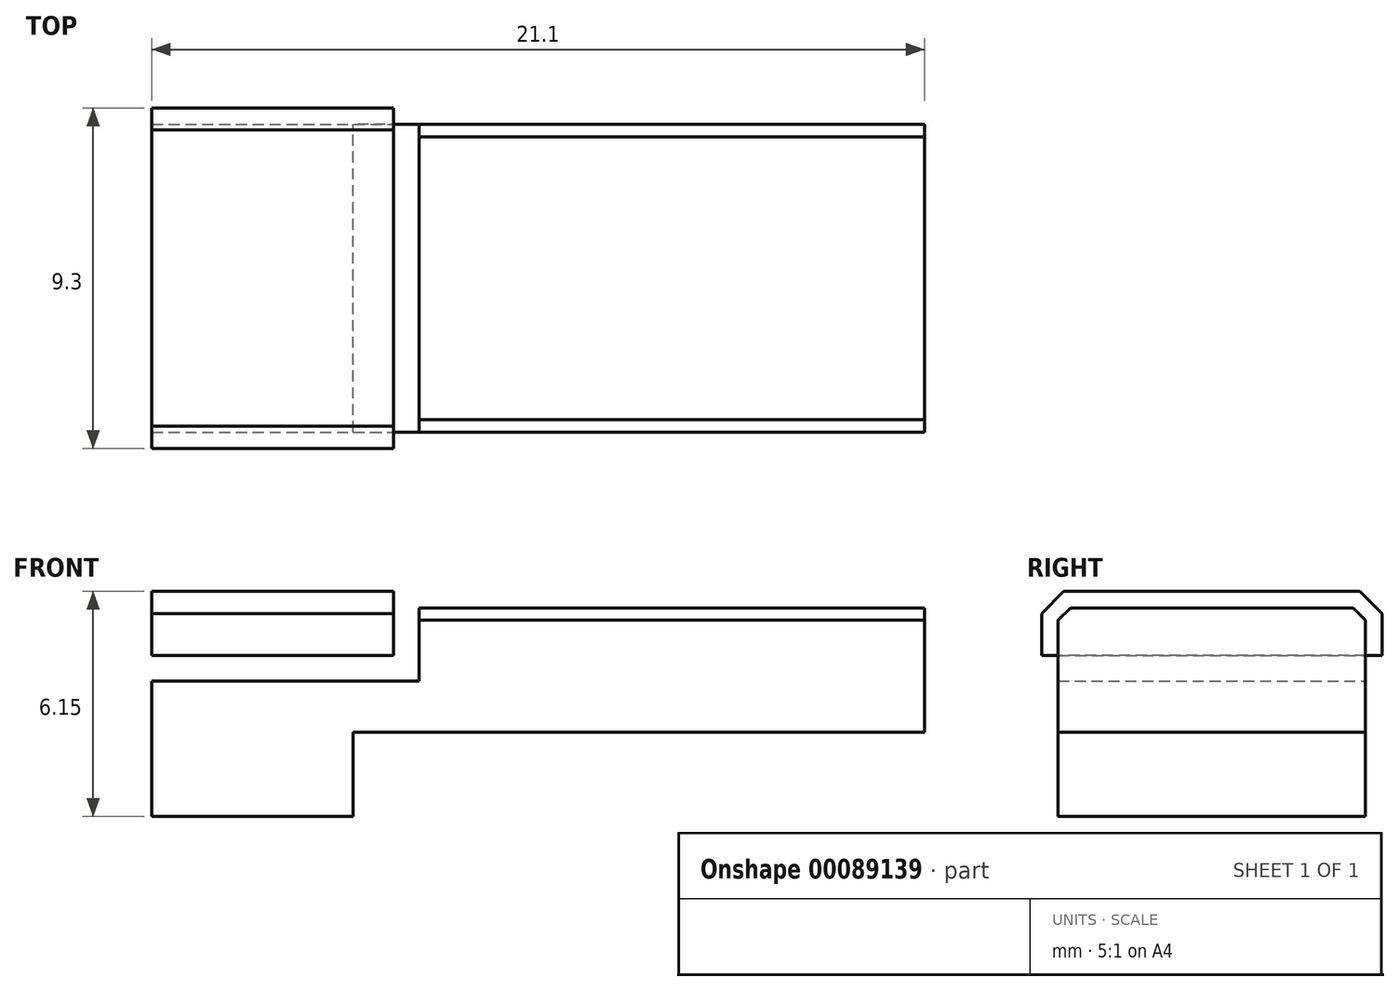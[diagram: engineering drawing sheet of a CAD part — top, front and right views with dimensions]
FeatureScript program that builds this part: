
annotation { "Feature Type Name" : "Feature", "Feature Type Description" : "" }
export const myFeature = defineFeature(function(context is Context, id is Id, definition is map)
    precondition{}
    {
        {
            var Q0;
            Q0=qCreatedBy(makeId("Top.planeOp"),FACE);
            var sketch = newSketch(context, id + "F0", { "sketchPlane" : qUnion([Q0])});
            skLineSegment(sketch, "E0.bottom", {"start": v(0, -4.9) * mm, "end": v(23, -4.9) * mm});
            skLineSegment(sketch, "E0.top", {"start": v(0, 4.9) * mm, "end": v(23, 4.9) * mm});
            skLineSegment(sketch, "E0.left", {"start": v(0, -4.9) * mm, "end": v(0, 4.9) * mm});
            skLineSegment(sketch, "E0.right", {"start": v(23, -4.9) * mm, "end": v(23, 4.9) * mm});
            skSolve(sketch);
        }
        {
            var Q0;
            Q0 = qSketchRegion(id + "F0", true);
            extrude(context, id + "F1", {"entities" : qUnion([Q0]), "depth" : 5.1 * mm});
        }
        {
            var Q0;
            Q0=makeQuery(id+"F1.opExtrude","CAP_FACE",FACE,{"disambiguationData":[OSD([sQuery(id+"F0.wireOp",EDGE,"E0.bottom"),sQuery(id+"F0.wireOp",EDGE,"E0.top"),sQuery(id+"F0.wireOp",EDGE,"E0.left"),sQuery(id+"F0.wireOp",EDGE,"E0.right")])],"isStart":false});
            var sketch = newSketch(context, id + "F2", { "sketchPlane" : qUnion([Q0])});
            skLineSegment(sketch, "E1.top", {"start": v(23, -4.9) * mm, "end": v(7.3, -4.9) * mm});
            skLineSegment(sketch, "E1.left", {"start": v(23, 4.9) * mm, "end": v(23, -4.9) * mm});
            skLineSegment(sketch, "E1.right", {"start": v(7.3, 4.9) * mm, "end": v(7.3, -4.9) * mm});
            skLineSegment(sketch, "E2.0", {"start": v(0, -4.9) * mm, "end": v(0, 4.9) * mm, "construction": true});
            skSolve(sketch);
        }
        {
            var Q0;
            Q0=makeQuery(id+"F2.imprint","IMPRINT",FACE,{"disambiguationData":[TD([[makeQuery(id+"F2.imprint","IMPRINT",EDGE,{"derivedFrom":sQuery(id+"F2.wireOp",EDGE,"E1.top")}),1.0]])]});
            extrude(context, id + "F3", {"entities" : qUnion([Q0]), "operationType" : NewBodyOperationType.ADD, "depth" : 2 * mm});
        }
        {
            var Q0;
            Q0=makeQuery(id+"F1.opExtrude","CAP_FACE",FACE,{"disambiguationData":[OSD([sQuery(id+"F0.wireOp",EDGE,"E0.bottom"),sQuery(id+"F0.wireOp",EDGE,"E0.top"),sQuery(id+"F0.wireOp",EDGE,"E0.left"),sQuery(id+"F0.wireOp",EDGE,"E0.right")])],"isStart":true});
            var sketch = newSketch(context, id + "F4", { "sketchPlane" : qUnion([Q0])});
            skLineSegment(sketch, "E3.bottom", {"start": v(6.2, 4.5) * mm, "end": v(22.2, 4.5) * mm});
            skLineSegment(sketch, "E3.top", {"start": v(6.2, -4.5) * mm, "end": v(22.2, -4.5) * mm});
            skLineSegment(sketch, "E3.left", {"start": v(6.2, 4.5) * mm, "end": v(6.2, -4.5) * mm});
            skLineSegment(sketch, "E3.right", {"start": v(22.2, 4.5) * mm, "end": v(22.2, -4.5) * mm});
            skSolve(sketch);
        }
        {
            var Q0;
            Q0 = qSketchRegion(id + "F4", true);
            extrude(context, id + "F5", {"entities" : qUnion([Q0]), "operationType" : NewBodyOperationType.REMOVE, "oppositeDirection" : true, "depth" : 3 * mm});
        }
        {
            var Q0;
            Q0=makeQuery(id+"F3.opExtrude","CAP_EDGE",EDGE,{"disambiguationData":[OSD([sQuery(id+"F2.wireOp",EDGE,"E1.top")])],"isStart":false});
            var Q1;
            Q1=makeQuery(id+"F3.opExtrude","CAP_EDGE",EDGE,{"disambiguationData":[OSD([sQuery(id+"F0.wireOp",EDGE,"E0.top")])],"isStart":false});
            chamfer(context, id + "F6", {"entities" : qUnion([Q0, Q1]), "width" : 0.75 * mm, "tangentPropagation" : true});
        }
        {
            var Q0;
            Q0=makeQuery(id+"F5.boolean.opBoolean","COPY",FACE,{"derivedFrom":makeQuery(id+"F5.opExtrude","CAP_FACE",FACE,{"disambiguationData":[OSD([sQuery(id+"F4.wireOp",EDGE,"E3.bottom"),sQuery(id+"F4.wireOp",EDGE,"E3.top"),sQuery(id+"F4.wireOp",EDGE,"E3.left"),sQuery(id+"F4.wireOp",EDGE,"E3.right")])],"isStart":false})});
            var Q1;
            Q1=makeQuery(id+"F5.boolean.opBoolean","COPY",FACE,{"derivedFrom":makeQuery(id+"F5.opExtrude","SWEPT_FACE",FACE,{"disambiguationData":[OSD([sQuery(id+"F4.wireOp",EDGE,"E3.left")])]})});
            shell(context, id + "F7", {"entities" : qUnion([Q0, Q1]), "thickness" : .7 * mm});
        }
        {
            var Q0;
            Q0=makeQuery(id+"F1.opExtrude","SWEPT_FACE",FACE,{"disambiguationData":[OSD([sQuery(id+"F0.wireOp",EDGE,"E0.left")])]});
            var sketch = newSketch(context, id + "F8", { "sketchPlane" : qUnion([Q0])});
            skCircle(sketch, "E4", {"center": v(-1.5, 3.4) * mm, "radius": 0.3 * mm});
            skCircle(sketch, "E5", {"center": v(1.5, 3.4) * mm, "radius": 0.3 * mm});
            skPoint(sketch, "E6", {"position": v(-1.52, 3.7) * mm});
            skPoint(sketch, "E7", {"position": v(1.52, 3.7) * mm});
            skSolve(sketch);
        }
        {
            var Q0;
            Q0 = qSketchRegion(id + "F8", true);
            extrude(context, id + "F9", {"entities" : qUnion([Q0]), "operationType" : NewBodyOperationType.REMOVE, "endBound" : BoundingType.UP_TO_NEXT, "oppositeDirection" : true, "depth" : 25 * mm});
        }
        {
            var Q0;
            Q0=makeQuery(id+"F1.opExtrude","CAP_EDGE",EDGE,{"disambiguationData":[OSD([sQuery(id+"F0.wireOp",EDGE,"E0.top")])],"isStart":true});
            var Q1;
            Q1=makeQuery(id+"F1.opExtrude","CAP_EDGE",EDGE,{"disambiguationData":[OSD([sQuery(id+"F0.wireOp",EDGE,"E0.bottom")])],"isStart":true});
            var Q2;
            Q2=makeQuery(id+"F1.opExtrude","CAP_EDGE",EDGE,{"disambiguationData":[OSD([sQuery(id+"F0.wireOp",EDGE,"E0.left")])],"isStart":false});
            var Q3;
            Q3=makeQuery(id+"F3.opExtrude","CAP_EDGE",EDGE,{"disambiguationData":[OSD([sQuery(id+"F2.wireOp",EDGE,"E1.right")])],"isStart":false});
            var Q4;
            Q4=makeQuery(id+"F1.opExtrude","CAP_EDGE",EDGE,{"disambiguationData":[OSD([sQuery(id+"F0.wireOp",EDGE,"E0.bottom")])],"isStart":false});
            var Q5;
            Q5=makeQuery(id+"F1.opExtrude","CAP_EDGE",EDGE,{"disambiguationData":[OSD([sQuery(id+"F0.wireOp",EDGE,"E0.top")])],"isStart":false});
            var Q6;
            Q6=makeQuery(id+"F3.opExtrude","SWEPT_EDGE",EDGE,{"disambiguationData":[OSD([sQuery(id+"F0.wireOp",EDGE,"E0.top"),sQuery(id+"F2.wireOp",EDGE,"E1.right")])]});
            var Q7;
            Q7=makeQuery(id+"F3.opExtrude","SWEPT_EDGE",EDGE,{"disambiguationData":[OSD([sQuery(id+"F0.wireOp",EDGE,"E0.bottom"),sQuery(id+"F2.wireOp",EDGE,"E1.top"),sQuery(id+"F2.wireOp",EDGE,"E1.right")])]});
            var Q8;
            Q8=makeQuery(id+"F6.opChamfer","BLEND_EDGE",EDGE,{"blendedFrom":[makeQuery(id+"F3.opExtrude","CAP_EDGE",EDGE,{"disambiguationData":[OSD([sQuery(id+"F0.wireOp",EDGE,"E0.top")])],"isStart":false}),makeQuery(id+"F3.opExtrude","SWEPT_FACE",FACE,{"disambiguationData":[OSD([sQuery(id+"F2.wireOp",EDGE,"E1.right")])]})],"blendedInto":[makeQuery(id+"F3.opExtrude","SWEPT_FACE",FACE,{"disambiguationData":[OSD([sQuery(id+"F2.wireOp",EDGE,"E1.right")])]})]});
            var Q9;
            Q9=makeQuery(id+"F6.opChamfer","BLEND_EDGE",EDGE,{"blendedFrom":[makeQuery(id+"F3.opExtrude","CAP_EDGE",EDGE,{"disambiguationData":[OSD([sQuery(id+"F2.wireOp",EDGE,"E1.top")])],"isStart":false}),makeQuery(id+"F3.opExtrude","SWEPT_FACE",FACE,{"disambiguationData":[OSD([sQuery(id+"F2.wireOp",EDGE,"E1.right")])]})],"blendedInto":[makeQuery(id+"F3.opExtrude","SWEPT_FACE",FACE,{"disambiguationData":[OSD([sQuery(id+"F2.wireOp",EDGE,"E1.right")])]})]});
            var Q10;
            Q10=makeQuery(id+"F1.opExtrude","SWEPT_EDGE",EDGE,{"disambiguationData":[OSD([sQuery(id+"F0.wireOp",EDGE,"E0.bottom"),sQuery(id+"F0.wireOp",EDGE,"E0.left")])]});
            var Q11;
            Q11=makeQuery(id+"F1.opExtrude","SWEPT_EDGE",EDGE,{"disambiguationData":[OSD([sQuery(id+"F0.wireOp",EDGE,"E0.top"),sQuery(id+"F0.wireOp",EDGE,"E0.left")])]});
            var Q12;
            Q12=makeQuery(id+"F3.boolean.opBoolean","MERGE",FACE,{"derivedFrom":[makeQuery(id+"F1.opExtrude","SWEPT_FACE",FACE,{"disambiguationData":[OSD([sQuery(id+"F0.wireOp",EDGE,"E0.right")])]}),makeQuery(id+"F3.opExtrude","SWEPT_FACE",FACE,{"disambiguationData":[OSD([sQuery(id+"F2.wireOp",EDGE,"E1.left")])]})]});
            var Q13;
            Q13=makeQuery(id+"F1.opExtrude","CAP_FACE",FACE,{"disambiguationData":[OSD([sQuery(id+"F0.wireOp",EDGE,"E0.bottom"),sQuery(id+"F0.wireOp",EDGE,"E0.top"),sQuery(id+"F0.wireOp",EDGE,"E0.left"),sQuery(id+"F0.wireOp",EDGE,"E0.right")])],"isStart":true});
            var Q14;
            Q14=makeQuery(id+"F3.opExtrude","CAP_EDGE",EDGE,{"disambiguationData":[OSD([sQuery(id+"F2.wireOp",EDGE,"E1.right")])],"isStart":true});
            chamfer(context, id + "F10", {"entities" : qUnion([Q0, Q1, Q2, Q3, Q4, Q5, Q6, Q7, Q8, Q9, Q10, Q11, Q12, Q13, Q14]), "width" : 0.25 * mm, "tangentPropagation" : true});
        }
        {
            var Q0;
            Q0=makeQuery(id+"F7.opShell","MERGE",FACE,{"derivedFrom":[makeQuery(id+"F5.boolean.opBoolean","COPY",FACE,{"derivedFrom":makeQuery(id+"F5.opExtrude","SWEPT_FACE",FACE,{"disambiguationData":[OSD([sQuery(id+"F4.wireOp",EDGE,"E3.right")])]})}),makeQuery(id+"F3.boolean.opBoolean","MERGE",FACE,{"derivedFrom":[makeQuery(id+"F1.opExtrude","SWEPT_FACE",FACE,{"disambiguationData":[OSD([sQuery(id+"F0.wireOp",EDGE,"E0.right")])]}),makeQuery(id+"F3.opExtrude","SWEPT_FACE",FACE,{"disambiguationData":[OSD([sQuery(id+"F2.wireOp",EDGE,"E1.left")])]})]})]});
            var sketch = newSketch(context, id + "F11", { "sketchPlane" : qUnion([Q0])});
            skLineSegment(sketch, "E8", {"start": v(4.2, 3) * mm, "end": v(-4.2, 3) * mm});
            skLineSegment(sketch, "E9.1", {"start": v(4.2, 6.06) * mm, "end": v(4.2, 3) * mm});
            skLineSegment(sketch, "E9.2", {"start": v(3.86, 6.4) * mm, "end": v(4.2, 6.06) * mm});
            skLineSegment(sketch, "E9.3", {"start": v(3.86, 6.4) * mm, "end": v(-3.84, 6.42) * mm});
            skLineSegment(sketch, "E9.4", {"start": v(-4.2, 6.06) * mm, "end": v(-3.84, 6.42) * mm});
            skLineSegment(sketch, "E9.5", {"start": v(-4.2, 6.06) * mm, "end": v(-4.2, 2.94) * mm});
            skSolve(sketch);
        }
        {
            var Q0;
            Q0=makeQuery(id+"F7.opShell","OFFSET_FACE",FACE,{"disambiguationData":[OSD([sQuery(id+"F0.wireOp",EDGE,"E0.right"),sQuery(id+"F2.wireOp",EDGE,"E1.left")])]});
            extrude(context, id + "F12", {"entities" : qUnion([Q0]), "operationType" : NewBodyOperationType.ADD, "depth" : 0.5 * mm});
        }
        {
            var Q0;
            Q0=makeQuery(id+"F11.imprint","IMPRINT",FACE,{"disambiguationData":[TD([[makeQuery(id+"F11.imprint","IMPRINT",EDGE,{"derivedFrom":sQuery(id+"F11.wireOp",EDGE,"E8")}),1.0]])]});
            var sketch = newSketch(context, id + "F13", { "sketchPlane" : qUnion([Q0])});
            skLineSegment(sketch, "E10.0.0", {"start": v(-4.65, 0.25) * mm, "end": v(-4.65, 6.25) * mm});
            skLineSegment(sketch, "E10.0.1", {"start": v(-4.65, 6.25) * mm, "end": v(-4.05, 6.85) * mm});
            skLineSegment(sketch, "E10.0.2", {"start": v(-4.05, 6.85) * mm, "end": v(4.05, 6.85) * mm});
            skLineSegment(sketch, "E10.0.3", {"start": v(4.05, 6.85) * mm, "end": v(4.65, 6.25) * mm});
            skLineSegment(sketch, "E10.0.4", {"start": v(4.65, 6.25) * mm, "end": v(4.65, 0.25) * mm});
            skLineSegment(sketch, "E10.0.5", {"start": v(4.65, 0.25) * mm, "end": v(-4.65, 0.25) * mm});
            skSolve(sketch);
        }
        {
            var Q0;
            Q0 = qSketchRegion(id + "F13", true);
            var Q1;
            Q1=makeQuery(id+"F7.opShell","OFFSET_FACE",FACE,{"disambiguationData":[OSD([sQuery(id+"F0.wireOp",EDGE,"E0.left")])]});
            extrude(context, id + "F14", {"entities" : qUnion([Q0]), "endBound" : BoundingType.UP_TO_SURFACE, "depth" : 25 * mm, "endBoundEntityFace" : qUnion([Q1]), "offsetDistance" : 25 * mm});
        }
        {
            var Q0;
            Q0=makeQuery(id+"F10.opChamfer","SPLIT",FACE,{"disambiguationData":[OD(0.0)],"derivedFrom":makeQuery(id+"F1.opExtrude","CAP_FACE",FACE,{"disambiguationData":[OSD([sQuery(id+"F0.wireOp",EDGE,"E0.bottom"),sQuery(id+"F0.wireOp",EDGE,"E0.top"),sQuery(id+"F0.wireOp",EDGE,"E0.left"),sQuery(id+"F0.wireOp",EDGE,"E0.right")])],"isStart":true})});
            var sketch = newSketch(context, id + "F15", { "sketchPlane" : qUnion([Q0])});
            skLineSegment(sketch, "E11.0", {"start": v(22.2, 4.5) * mm, "end": v(6.2, 4.5) * mm});
            skLineSegment(sketch, "E11.1", {"start": v(6.2, 4.5) * mm, "end": v(6.2, -4.5) * mm});
            skLineSegment(sketch, "E11.2", {"start": v(6.2, -4.5) * mm, "end": v(22.2, -4.5) * mm});
            skLineSegment(sketch, "E11.3", {"start": v(22.2, -4.5) * mm, "end": v(22.2, 4.5) * mm});
            skSolve(sketch);
        }
        {
            var Q0;
            Q0 = qSketchRegion(id + "F15", true);
            extrude(context, id + "F16", {"entities" : qUnion([Q0]), "operationType" : NewBodyOperationType.REMOVE, "oppositeDirection" : true, "depth" : 3 * mm, "offsetDistance" : 25 * mm});
        }
        {
            var Q0;
            Q0=makeQuery(id+"F1.opExtrude","SWEPT_BODY",BODY,{"disambiguationData":[OSD([sQuery(id+"F0.wireOp",EDGE,"E0.bottom"),sQuery(id+"F0.wireOp",EDGE,"E0.top"),sQuery(id+"F0.wireOp",EDGE,"E0.left"),sQuery(id+"F0.wireOp",EDGE,"E0.right")])]});
            var Q1;
            Q1=makeQuery(id+"F14.opExtrude","SWEPT_BODY",BODY,{"disambiguationData":[OSD([sQuery(id+"F13.wireOp",EDGE,"E10.0.0"),sQuery(id+"F13.wireOp",EDGE,"E10.0.1"),sQuery(id+"F13.wireOp",EDGE,"E10.0.2"),sQuery(id+"F13.wireOp",EDGE,"E10.0.3"),sQuery(id+"F13.wireOp",EDGE,"E10.0.4"),sQuery(id+"F13.wireOp",EDGE,"E10.0.5")])]});
            booleanBodies(context, id + "F17", {"operationType" : BooleanOperationType.SUBTRACTION, "tools" : qUnion([Q0]), "targets" : qUnion([Q1])});
        }
    });
